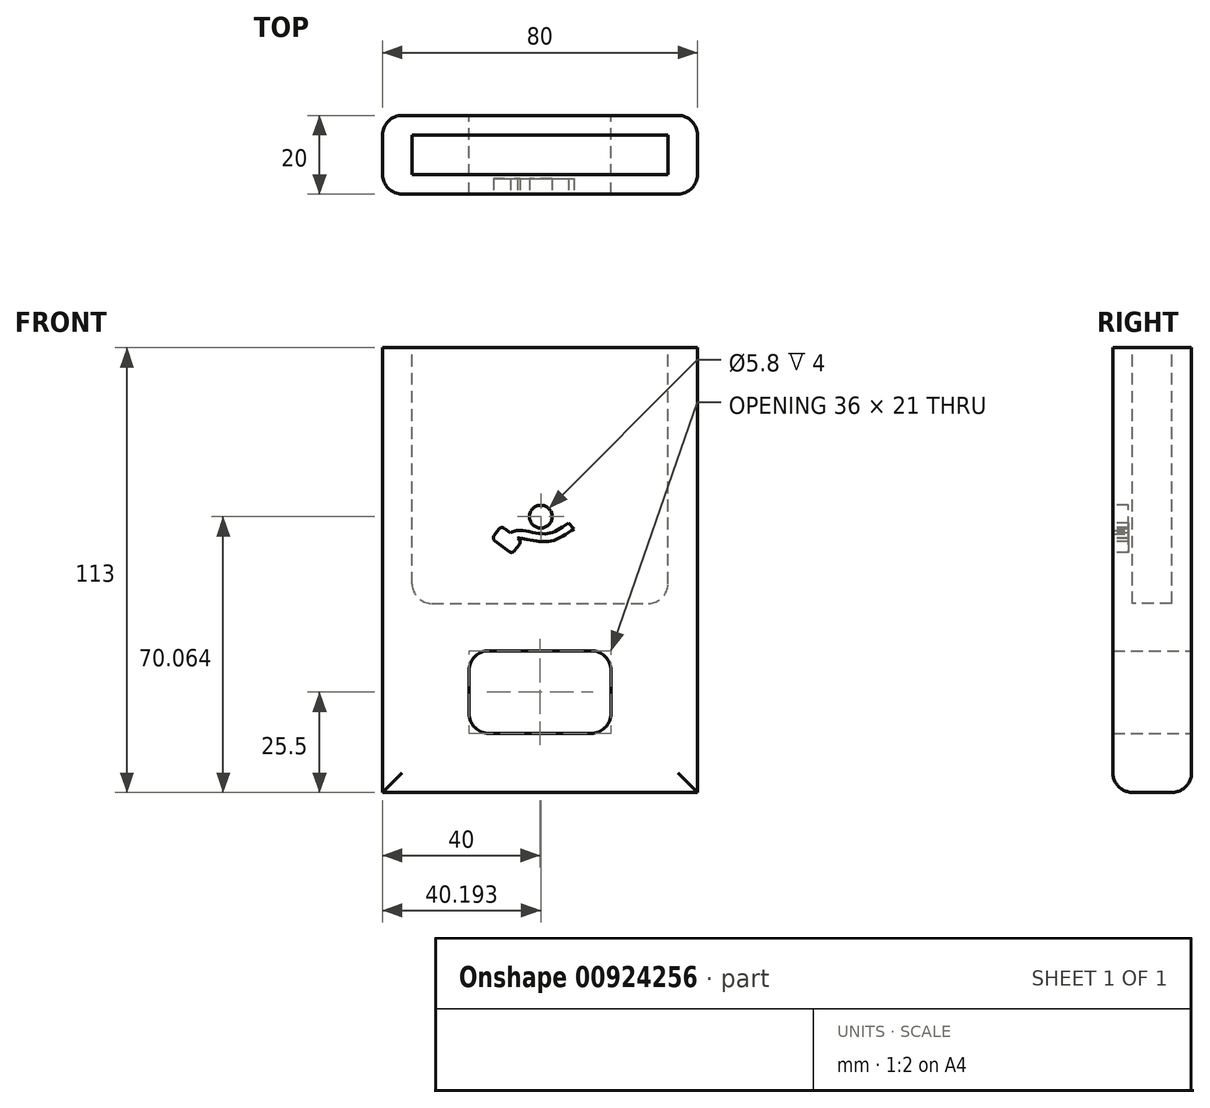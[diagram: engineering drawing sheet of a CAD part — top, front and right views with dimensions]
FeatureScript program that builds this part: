
annotation { "Feature Type Name" : "Feature", "Feature Type Description" : "" }
export const myFeature = defineFeature(function(context is Context, id is Id, definition is map)
    precondition{}
    {
        {
            var Q0;
            Q0=qCreatedBy(makeId("Front.planeOp"),FACE);
            var sketch = newSketch(context, id + "F0", { "sketchPlane" : qUnion([Q0])});
            skLineSegment(sketch, "E0.top", {"start": v(-80, 0) * mm, "end": v(0, 0) * mm});
            skLineSegment(sketch, "E0.left", {"start": v(-80, 113) * mm, "end": v(-80, 0) * mm});
            skLineSegment(sketch, "E0.right", {"start": v(0, 113) * mm, "end": v(0, 0) * mm});
            skLineSegment(sketch, "E1.bottom", {"start": v(-58, 15) * mm, "end": v(-22, 15) * mm});
            skLineSegment(sketch, "E1.left", {"start": v(-58, 15) * mm, "end": v(-58, 36) * mm});
            skLineSegment(sketch, "E1.right", {"start": v(-22, 15) * mm, "end": v(-22, 36) * mm});
            skLineSegment(sketch, "E2", {"start": v(-80, 113) * mm, "end": v(0, 113) * mm});
            skLineSegment(sketch, "E3", {"start": v(-22, 36) * mm, "end": v(-58, 36) * mm});
            skSolve(sketch);
        }
        {
            var Q0;
            Q0 = qSketchRegion(id + "F0", true);
            extrude(context, id + "F1", {"entities" : qUnion([Q0]), "depth" : 20 * mm, "offsetDistance" : 25 * mm});
        }
        {
            var Q0;
            Q0=makeQuery(id+"F1.opExtrude","SWEPT_FACE",FACE,{"disambiguationData":[OSD([sQuery(id+"F0.wireOp",EDGE,"E2")])]});
            cPlane(context, id + "F2", {"entities" : qUnion([Q0]), "cplaneType" : CPlaneType.OFFSET, "offset" : 0 * mm, "width" : 150 * mm, "height" : 150 * mm});
        }
        {
            var Q0;
            Q0=qCreatedBy(id+"F2.planeOp",FACE);
            var sketch = newSketch(context, id + "F3", { "sketchPlane" : qUnion([Q0])});
            skLineSegment(sketch, "E4.bottom", {"start": v(0, 0) * mm, "end": v(-80, 0) * mm});
            skLineSegment(sketch, "E4.top", {"start": v(0, -20) * mm, "end": v(-80, -20) * mm});
            skLineSegment(sketch, "E4.left", {"start": v(0, 0) * mm, "end": v(0, -20) * mm});
            skLineSegment(sketch, "E4.right", {"start": v(-80, 0) * mm, "end": v(-80, -20) * mm});
            skLineSegment(sketch, "E5.bottom", {"start": v(-72.5, -5) * mm, "end": v(-7.5, -5) * mm});
            skLineSegment(sketch, "E5.top", {"start": v(-72.5, -15) * mm, "end": v(-7.5, -15) * mm});
            skLineSegment(sketch, "E5.left", {"start": v(-72.5, -5) * mm, "end": v(-72.5, -15) * mm});
            skLineSegment(sketch, "E5.right", {"start": v(-7.5, -5) * mm, "end": v(-7.5, -15) * mm});
            skSolve(sketch);
        }
        {
            var Q0;
            Q0=makeQuery(id+"F3.imprint","IMPRINT",FACE,{"disambiguationData":[TD([[makeQuery(id+"F3.imprint","IMPRINT",EDGE,{"derivedFrom":sQuery(id+"F3.wireOp",EDGE,"E5.bottom")}),-1.0]])]});
            extrude(context, id + "F4", {"entities" : qUnion([Q0]), "operationType" : NewBodyOperationType.REMOVE, "oppositeDirection" : true, "depth" : 65 * mm, "offsetDistance" : 25 * mm});
        }
        {
            var Q0;
            Q0=makeQuery(id+"F1.opExtrude","CAP_FACE",FACE,{"disambiguationData":[OSD([sQuery(id+"F0.wireOp",EDGE,"E0.top"),sQuery(id+"F0.wireOp",EDGE,"E0.left"),sQuery(id+"F0.wireOp",EDGE,"E0.right"),sQuery(id+"F0.wireOp",EDGE,"E1.bottom"),sQuery(id+"F0.wireOp",EDGE,"E1.left"),sQuery(id+"F0.wireOp",EDGE,"E1.right"),sQuery(id+"F0.wireOp",EDGE,"E2"),sQuery(id+"F0.wireOp",EDGE,"E3")])],"isStart":false});
            cPlane(context, id + "F5", {"entities" : qUnion([Q0]), "cplaneType" : CPlaneType.OFFSET, "offset" : 0 * mm, "width" : 150 * mm, "height" : 150 * mm});
        }
        {
            var Q0;
            Q0=qCreatedBy(id+"F5.planeOp",FACE);
            var sketch = newSketch(context, id + "F6", { "sketchPlane" : qUnion([Q0])});
            skLineSegment(sketch, "E6", {"start": v(-62.56, 79.41) * mm, "end": v(-62.56, 79.41) * mm});
            skFitSpline(sketch, "E7", {"points": [v(-48.17, 65.78) * mm, v(-45.66, 66.6) * mm, v(-38.51, 65.71) * mm, v(-31.1, 69.37) * mm], "startDerivative": vector(15.74, 3.2) * mm, "endDerivative": vector(27.25, 14.63) * mm});
            skFitSpline(sketch, "E8", {"points": [v(-50.8, 60.12) * mm, v(-43.4, 58.27) * mm, v(-38.96, 61) * mm, v(-32.5, 62.96) * mm, v(-28.23, 56.64) * mm], "startDerivative": vector(23.02, -28.98) * mm, "endDerivative": vector(3.27, -41.53) * mm});
            skLineSegment(sketch, "E9.bottom", {"start": v(-49.09, 67.08) * mm, "end": v(-45.47, 64.4) * mm});
            skLineSegment(sketch, "E9.top", {"start": v(-51.46, 63.86) * mm, "end": v(-47.84, 61.2) * mm});
            skLineSegment(sketch, "E9.left", {"start": v(-50.48, 66.87) * mm, "end": v(-51.67, 65.26) * mm});
            skLineSegment(sketch, "E9.right", {"start": v(-45.25, 63.01) * mm, "end": v(-46.44, 61.4) * mm});
            skPoint(sketch, "E10.visualSharp", {"position": v(-49.9, 67.67) * mm});
            skArc(sketch, "E10.filletArc", {"start": v(-49.09, 67.08) * mm, "mid": v(-49.83, 67.26) * mm, "end": v(-50.48, 66.87) * mm});
            skPoint(sketch, "E11.visualSharp", {"position": v(-52.27, 64.46) * mm});
            skArc(sketch, "E11.filletArc", {"start": v(-51.67, 65.26) * mm, "mid": v(-51.86, 64.52) * mm, "end": v(-51.46, 63.86) * mm});
            skPoint(sketch, "E12.visualSharp", {"position": v(-44.66, 63.82) * mm});
            skArc(sketch, "E12.filletArc", {"start": v(-45.25, 63.01) * mm, "mid": v(-45.07, 63.75) * mm, "end": v(-45.47, 64.4) * mm});
            skPoint(sketch, "E13.visualSharp", {"position": v(-47.84, 61.2) * mm});
            skArc(sketch, "E13.filletArc", {"start": v(-47.84, 61.2) * mm, "mid": v(-47.1, 61) * mm, "end": v(-46.44, 61.4) * mm});
            skLineSegment(sketch, "E14", {"start": v(-32.75, 68.42) * mm, "end": v(-31.33, 66.94) * mm});
            skFitSpline(sketch, "E15.0", {"points": [v(-52.36, 58.88) * mm, v(-52.04, 58.48) * mm, v(-51.36, 57.77) * mm, v(-50.22, 56.95) * mm, v(-49, 56.37) * mm, v(-47.37, 55.9) * mm, v(-45.37, 55.79) * mm, v(-43.56, 56.1) * mm, v(-42.28, 56.53) * mm, v(-41.13, 57.05) * mm, v(-39.94, 57.81) * mm, v(-38.75, 58.71) * mm, v(-37.6, 59.53) * mm, v(-36.23, 60.3) * mm, v(-35.05, 60.76) * mm, v(-34.18, 60.98) * mm, v(-33.59, 61.05) * mm, v(-33.08, 61.04) * mm, v(-32.67, 60.96) * mm, v(-32.28, 60.8) * mm, v(-31.78, 60.48) * mm, v(-31.16, 59.83) * mm, v(-30.53, 58.49) * mm, v(-30.28, 57.21) * mm, v(-30.22, 56.48) * mm]});
            skLineSegment(sketch, "E16", {"start": v(-50.8, 60.12) * mm, "end": v(-52.2, 58.68) * mm});
            skLineSegment(sketch, "E17", {"start": v(-30.23, 56.64) * mm, "end": v(-28.23, 56.64) * mm});
            skCircle(sketch, "E18.0", {"center": v(-39.8, 70.06) * mm, "radius": 2.9 * mm});
            skFitSpline(sketch, "E19.0", {"points": [v(-47.77, 63.82) * mm, v(-47.54, 63.87) * mm, v(-47.12, 63.98) * mm, v(-46.58, 64.17) * mm, v(-46.16, 64.36) * mm, v(-45.88, 64.5) * mm, v(-45.7, 64.57) * mm, v(-45.65, 64.59) * mm, v(-45.6, 64.6) * mm, v(-45.56, 64.6) * mm, v(-45.5, 64.6) * mm, v(-45.39, 64.6) * mm, v(-45.24, 64.6) * mm, v(-45, 64.58) * mm, v(-44.62, 64.53) * mm, v(-44.1, 64.44) * mm, v(-43.31, 64.3) * mm, v(-42.2, 64.08) * mm, v(-41.02, 63.87) * mm, v(-40.05, 63.75) * mm, v(-39.3, 63.7) * mm, v(-38.67, 63.7) * mm, v(-38.16, 63.73) * mm, v(-37.42, 63.81) * mm, v(-36.36, 64.07) * mm, v(-35.12, 64.62) * mm, v(-34, 65.27) * mm, v(-32.88, 65.99) * mm, v(-31.65, 66.76) * mm, v(-30.68, 67.32) * mm, v(-30.15, 67.6) * mm]});
            skSolve(sketch);
        }
        {
            var Q0;
            Q0 = qSketchRegion(id + "F6", true);
            extrude(context, id + "F7", {"entities" : qUnion([Q0]), "operationType" : NewBodyOperationType.REMOVE, "oppositeDirection" : true, "depth" : 4 * mm, "offsetDistance" : 25 * mm});
        }
        {
            var Q0;
            Q0=makeQuery(id+"F1.opExtrude","SWEPT_EDGE",EDGE,{"disambiguationData":[OSD([sQuery(id+"F0.wireOp",EDGE,"E1.left"),sQuery(id+"F0.wireOp",EDGE,"E3")])]});
            var Q1;
            Q1=makeQuery(id+"F1.opExtrude","SWEPT_EDGE",EDGE,{"disambiguationData":[OSD([sQuery(id+"F0.wireOp",EDGE,"E1.right"),sQuery(id+"F0.wireOp",EDGE,"E3")])]});
            var Q2;
            Q2=makeQuery(id+"F1.opExtrude","SWEPT_EDGE",EDGE,{"disambiguationData":[OSD([sQuery(id+"F0.wireOp",EDGE,"E1.bottom"),sQuery(id+"F0.wireOp",EDGE,"E1.left")])]});
            var Q3;
            Q3=makeQuery(id+"F1.opExtrude","SWEPT_EDGE",EDGE,{"disambiguationData":[OSD([sQuery(id+"F0.wireOp",EDGE,"E1.bottom"),sQuery(id+"F0.wireOp",EDGE,"E1.right")])]});
            var Q4;
            Q4=makeQuery(id+"F4.boolean.opBoolean","COPY",EDGE,{"derivedFrom":makeQuery(id+"F4.opExtrude","CAP_EDGE",EDGE,{"disambiguationData":[OSD([sQuery(id+"F3.wireOp",EDGE,"E5.left")])],"isStart":false})});
            var Q5;
            Q5=makeQuery(id+"F4.boolean.opBoolean","COPY",EDGE,{"derivedFrom":makeQuery(id+"F4.opExtrude","CAP_EDGE",EDGE,{"disambiguationData":[OSD([sQuery(id+"F3.wireOp",EDGE,"E5.right")])],"isStart":false})});
            var Q6;
            Q6=makeQuery(id+"F1.opExtrude","CAP_EDGE",EDGE,{"disambiguationData":[OSD([sQuery(id+"F0.wireOp",EDGE,"E0.right")])],"isStart":true});
            var Q7;
            Q7=makeQuery(id+"F1.opExtrude","CAP_EDGE",EDGE,{"disambiguationData":[OSD([sQuery(id+"F0.wireOp",EDGE,"E0.right")])],"isStart":false});
            var Q8;
            Q8=makeQuery(id+"F1.opExtrude","CAP_EDGE",EDGE,{"disambiguationData":[OSD([sQuery(id+"F0.wireOp",EDGE,"E0.left")])],"isStart":true});
            var Q9;
            Q9=makeQuery(id+"F1.opExtrude","CAP_EDGE",EDGE,{"disambiguationData":[OSD([sQuery(id+"F0.wireOp",EDGE,"E0.left")])],"isStart":false});
            var Q10;
            Q10=makeQuery(id+"F1.opExtrude","CAP_EDGE",EDGE,{"disambiguationData":[OSD([sQuery(id+"F0.wireOp",EDGE,"E0.top")])],"isStart":true});
            var Q11;
            Q11=makeQuery(id+"F1.opExtrude","CAP_EDGE",EDGE,{"disambiguationData":[OSD([sQuery(id+"F0.wireOp",EDGE,"E0.top")])],"isStart":false});
            fillet(context, id + "F8", {"entities" : qUnion([Q0, Q1, Q2, Q3, Q4, Q5, Q6, Q7, Q8, Q9, Q10, Q11]), "radius" : 5 * mm, "tangentPropagation" : true, "allowEdgeOverflow" : false});
        }
    });
